# Revit family: RN 90077 Optifitt-Serra-Réduction
name_source: partatom
category: Rohrformteile
units: mm (PartAtom-declared; Revit-internal decimal feet)

## family parameters
Arbeitsebenenbasiert = Nein
Beim Laden mit Abzugskörper schneiden = Nein
Bemaßung runder Anschluss = Durchmesser verwenden
Gemeinsam genutzt = Nein
Immer vertikal = Ja
Teiletyp = Übergang

## types (12) — shared parameters
1.010.00.2 Blattnummer der Richtlinie = 29
1.010.00.3 Ausgabedatum (Monat) der Richtlinie = 201308
1.010.00.4 Herstellername = R. Nussbaum AG
1.010.00.5 Revisionsdatum der Datei = 20190521
1.010.00.6 Webadresse des Herstellers = http://www.nussbaum.ch
1.100.00.4 Produktbezeichnung = Versorgung
1.110.00.2 Index = 3
1.110.00.4 Produktbezeichnung = Optifitt-Serra
1.960/3L.00.8 Link (URL) = https://www.nussbaum.ch
29.700.00.4 Produktname = Optifitt-Serra-Reduktion
29.700.00.5 Produktkennung = 2
29.700.00.6 Querschnittsform = 1
29.700.00.7 Nennweitensystem = DN
29.700.00.8 Nenndrucksystem = PN
29.710.02.4 Nenndruck = 16
29.710.02.5 max. zul. Überdruck [hPa] = 1600
29.710.02.7 max. zul. Dauer-Betriebsdruck [hPa] = 1600
29.710.02.9 max. zul. Dauer-Betriebstemperatur [°C] = 90
Connector Visibility = Nein
EnclosingSpace Visibility = Nein

## per-type parameters (varying)
- DN=50x32: 1.800.00.3 TGA-Nummer=01900300000000000000000000000000000000000000000014000000000000000046; 1.800.00.4 Kommentarfeld=90077.40, Optifitt-Serra-Reduktion, DN=50x32, L=36, R=2, Rp=1¼; 1.810.00.3 Hersteller-Bestellnummer=90077.4; 1.810.00.4 DATANORM-Nummer=90077.4; 1.810.00.5 StLB-Nummer=214.537; 1.810.00.6 GTIN-Nummer=7612945680211; 29.710.02.10 Formstück-Gewicht [kg]=0.349; 29.710.02.3 Benennung=Optifitt-Serra-Reduktion, DN=50x32, L=36, R=2, Rp=1¼; CONNECTOR0_DIAMETER_dX_0r=32 mm; CONNECTOR0_dX_01=19 mm; CONNECTOR0_ref_dX=19 mm; CONNECTOR1_DIAMETER_dX_0r=50 mm; CONNECTOR1_dX_00=12 mm  [stored 0.0393701 ft]; CONNECTOR1_dX_01=36 mm; CONNECTOR1_ref_dX=36 mm; Hersteller=R. Nussbaum AG; Modell=90077.4; R. Nussbaum AG 90077.23 de Visibility=Nein; R. Nussbaum AG 90077.26 de Visibility=Nein; R. Nussbaum AG 90077.28 de Visibility=Nein; R. Nussbaum AG 90077.29 de Visibility=Nein; R. Nussbaum AG 90077.31 de Visibility=Nein; R. Nussbaum AG 90077.32 de Visibility=Nein; R. Nussbaum AG 90077.35 de Visibility=Nein; R. Nussbaum AG 90077.36 de Visibility=Nein; R. Nussbaum AG 90077.40 de Visibility=Ja; R. Nussbaum AG 90077.41 de Visibility=Nein; R. Nussbaum AG 90077.43 de Visibility=Nein; R. Nussbaum AG 90077.44 de Visibility=Nein; Typenkommentare=Optifitt-Serra-Réduction  DN=50x32; URL=https://www.nussbaum.ch
- DN=80x65: 1.800.00.3 TGA-Nummer=01900300000000000000000000000000000000000000000014000000000000000035; 1.800.00.4 Kommentarfeld=90077.44, Optifitt-Serra-Reduktion, DN=80x65, L=47, R=3, Rp=2½; 1.810.00.3 Hersteller-Bestellnummer=90077.44; 1.810.00.4 DATANORM-Nummer=90077.44; 1.810.00.6 GTIN-Nummer=7612945680242; 29.710.02.10 Formstück-Gewicht [kg]=0.757; 29.710.02.3 Benennung=Optifitt-Serra-Reduktion, DN=80x65, L=47, R=3, Rp=2½; CONNECTOR0_DIAMETER_dX_0r=65 mm; CONNECTOR0_dX_01=27 mm; CONNECTOR0_ref_dX=27 mm; CONNECTOR1_DIAMETER_dX_0r=80 mm; CONNECTOR1_dX_00=17 mm; CONNECTOR1_dX_01=47 mm; CONNECTOR1_ref_dX=47 mm; Hersteller=R. Nussbaum AG; Modell=90077.44; R. Nussbaum AG 90077.23 de Visibility=Nein; R. Nussbaum AG 90077.26 de Visibility=Nein; R. Nussbaum AG 90077.28 de Visibility=Nein; R. Nussbaum AG 90077.29 de Visibility=Nein; R. Nussbaum AG 90077.31 de Visibility=Nein; R. Nussbaum AG 90077.32 de Visibility=Nein; R. Nussbaum AG 90077.35 de Visibility=Nein; R. Nussbaum AG 90077.36 de Visibility=Nein; R. Nussbaum AG 90077.40 de Visibility=Nein; R. Nussbaum AG 90077.41 de Visibility=Nein; R. Nussbaum AG 90077.43 de Visibility=Nein; R. Nussbaum AG 90077.44 de Visibility=Ja; Typenkommentare=Optifitt-Serra-Réduction  DN=80x65; URL=https://www.nussbaum.ch
- DN=65x50: 1.800.00.3 TGA-Nummer=01900300000000000000000000000000000000000000000014000000000000000034; 1.800.00.4 Kommentarfeld=90077.43, Optifitt-Serra-Reduktion, DN=65x50, L=45, R=2½, Rp=2; 1.810.00.3 Hersteller-Bestellnummer=90077.43; 1.810.00.4 DATANORM-Nummer=90077.43; 1.810.00.5 StLB-Nummer=214.538; 1.810.00.6 GTIN-Nummer=7612945680235; 29.710.02.10 Formstück-Gewicht [kg]=0.629; 29.710.02.3 Benennung=Optifitt-Serra-Reduktion, DN=65x50, L=45, R=2½, Rp=2; CONNECTOR0_DIAMETER_dX_0r=50 mm; CONNECTOR0_dX_01=24 mm; CONNECTOR0_ref_dX=24 mm; CONNECTOR1_DIAMETER_dX_0r=65 mm; CONNECTOR1_dX_00=18 mm; CONNECTOR1_dX_01=45 mm  [stored 0.147638 ft]; CONNECTOR1_ref_dX=45 mm  [stored 0.147638 ft]; Hersteller=R. Nussbaum AG; Modell=90077.43; R. Nussbaum AG 90077.23 de Visibility=Nein; R. Nussbaum AG 90077.26 de Visibility=Nein; R. Nussbaum AG 90077.28 de Visibility=Nein; R. Nussbaum AG 90077.29 de Visibility=Nein; R. Nussbaum AG 90077.31 de Visibility=Nein; R. Nussbaum AG 90077.32 de Visibility=Nein; R. Nussbaum AG 90077.35 de Visibility=Nein; R. Nussbaum AG 90077.36 de Visibility=Nein; R. Nussbaum AG 90077.40 de Visibility=Nein; R. Nussbaum AG 90077.41 de Visibility=Nein; R. Nussbaum AG 90077.43 de Visibility=Ja; R. Nussbaum AG 90077.44 de Visibility=Nein; Typenkommentare=Optifitt-Serra-Réduction  DN=65x50; URL=https://www.nussbaum.ch
- DN=50x40: 1.800.00.3 TGA-Nummer=01900300000000000000000000000000000000000000000014000000000000000033; 1.800.00.4 Kommentarfeld=90077.41, Optifitt-Serra-Reduktion, DN=50x40, L=36, R=2, Rp=1½; 1.810.00.3 Hersteller-Bestellnummer=90077.41; 1.810.00.4 DATANORM-Nummer=90077.41; 1.810.00.5 StLB-Nummer=214.537; 1.810.00.6 GTIN-Nummer=7612945680228; 29.710.02.10 Formstück-Gewicht [kg]=0.295; 29.710.02.3 Benennung=Optifitt-Serra-Reduktion, DN=50x40, L=36, R=2, Rp=1½; CONNECTOR0_DIAMETER_dX_0r=40 mm; CONNECTOR0_dX_01=19 mm; CONNECTOR0_ref_dX=19 mm; CONNECTOR1_DIAMETER_dX_0r=50 mm; CONNECTOR1_dX_00=12 mm  [stored 0.0393701 ft]; CONNECTOR1_dX_01=36 mm; CONNECTOR1_ref_dX=36 mm; Hersteller=R. Nussbaum AG; Modell=90077.41; R. Nussbaum AG 90077.23 de Visibility=Nein; R. Nussbaum AG 90077.26 de Visibility=Nein; R. Nussbaum AG 90077.28 de Visibility=Nein; R. Nussbaum AG 90077.29 de Visibility=Nein; R. Nussbaum AG 90077.31 de Visibility=Nein; R. Nussbaum AG 90077.32 de Visibility=Nein; R. Nussbaum AG 90077.35 de Visibility=Nein; R. Nussbaum AG 90077.36 de Visibility=Nein; R. Nussbaum AG 90077.40 de Visibility=Nein; R. Nussbaum AG 90077.41 de Visibility=Ja; R. Nussbaum AG 90077.43 de Visibility=Nein; R. Nussbaum AG 90077.44 de Visibility=Nein; Typenkommentare=Optifitt-Serra-Réduction  DN=50x40; URL=https://www.nussbaum.ch
- DN=40x32: 1.800.00.3 TGA-Nummer=01900300000000000000000000000000000000000000000014000000000000000032; 1.800.00.4 Kommentarfeld=90077.36, Optifitt-Serra-Reduktion, DN=40x32, L=36, R=1½, Rp=1¼; 1.810.00.3 Hersteller-Bestellnummer=90077.36; 1.810.00.4 DATANORM-Nummer=90077.36; 1.810.00.5 StLB-Nummer=214.536; 1.810.00.6 GTIN-Nummer=7612945680204; 29.710.02.10 Formstück-Gewicht [kg]=0.2; 29.710.02.3 Benennung=Optifitt-Serra-Reduktion, DN=40x32, L=36, R=1½, Rp=1¼; CONNECTOR0_DIAMETER_dX_0r=32 mm; CONNECTOR0_dX_01=19 mm; CONNECTOR0_ref_dX=19 mm; CONNECTOR1_DIAMETER_dX_0r=40 mm; CONNECTOR1_dX_00=17 mm; CONNECTOR1_dX_01=36 mm; CONNECTOR1_ref_dX=36 mm; Hersteller=R. Nussbaum AG; Modell=90077.36; R. Nussbaum AG 90077.23 de Visibility=Nein; R. Nussbaum AG 90077.26 de Visibility=Nein; R. Nussbaum AG 90077.28 de Visibility=Nein; R. Nussbaum AG 90077.29 de Visibility=Nein; R. Nussbaum AG 90077.31 de Visibility=Nein; R. Nussbaum AG 90077.32 de Visibility=Nein; R. Nussbaum AG 90077.35 de Visibility=Nein; R. Nussbaum AG 90077.36 de Visibility=Ja; R. Nussbaum AG 90077.40 de Visibility=Nein; R. Nussbaum AG 90077.41 de Visibility=Nein; R. Nussbaum AG 90077.43 de Visibility=Nein; R. Nussbaum AG 90077.44 de Visibility=Nein; Typenkommentare=Optifitt-Serra-Réduction  DN=40x32; URL=https://www.nussbaum.ch
- DN=40x25: 1.800.00.3 TGA-Nummer=01900300000000000000000000000000000000000000000014000000000000000031; 1.800.00.4 Kommentarfeld=90077.35, Optifitt-Serra-Reduktion, DN=40x25, L=36, R=1½, Rp=1; 1.810.00.3 Hersteller-Bestellnummer=90077.35; 1.810.00.4 DATANORM-Nummer=90077.35; 1.810.00.5 StLB-Nummer=214.535; 1.810.00.6 GTIN-Nummer=7612945680198; 29.710.02.10 Formstück-Gewicht [kg]=0.001; 29.710.02.3 Benennung=Optifitt-Serra-Reduktion, DN=40x25, L=36, R=1½, Rp=1; CONNECTOR0_DIAMETER_dX_0r=25 mm  [stored 0.082021 ft]; CONNECTOR0_dX_01=17 mm; CONNECTOR0_ref_dX=17 mm; CONNECTOR1_DIAMETER_dX_0r=40 mm; CONNECTOR1_dX_00=17 mm; CONNECTOR1_dX_01=36 mm; CONNECTOR1_ref_dX=36 mm; Hersteller=R. Nussbaum AG; Modell=90077.35; R. Nussbaum AG 90077.23 de Visibility=Nein; R. Nussbaum AG 90077.26 de Visibility=Nein; R. Nussbaum AG 90077.28 de Visibility=Nein; R. Nussbaum AG 90077.29 de Visibility=Nein; R. Nussbaum AG 90077.31 de Visibility=Nein; R. Nussbaum AG 90077.32 de Visibility=Nein; R. Nussbaum AG 90077.35 de Visibility=Ja; R. Nussbaum AG 90077.36 de Visibility=Nein; R. Nussbaum AG 90077.40 de Visibility=Nein; R. Nussbaum AG 90077.41 de Visibility=Nein; R. Nussbaum AG 90077.43 de Visibility=Nein; R. Nussbaum AG 90077.44 de Visibility=Nein; Typenkommentare=Optifitt-Serra-Réduction  DN=40x25; URL=https://www.nussbaum.ch
- DN=32x25: 1.800.00.3 TGA-Nummer=01900300000000000000000000000000000000000000000014000000000000000030; 1.800.00.4 Kommentarfeld=90077.32, Optifitt-Serra-Reduktion, DN=32x25, L=30, R=1¼, Rp=1; 1.810.00.3 Hersteller-Bestellnummer=90077.32; 1.810.00.4 DATANORM-Nummer=90077.32; 1.810.00.5 StLB-Nummer=214.535; 1.810.00.6 GTIN-Nummer=7612945680259; 29.710.02.10 Formstück-Gewicht [kg]=0.139; 29.710.02.3 Benennung=Optifitt-Serra-Reduktion, DN=32x25, L=30, R=1¼, Rp=1; CONNECTOR0_DIAMETER_dX_0r=25 mm  [stored 0.082021 ft]; CONNECTOR0_dX_01=17 mm; CONNECTOR0_ref_dX=17 mm; CONNECTOR1_DIAMETER_dX_0r=32 mm; CONNECTOR1_dX_00=11 mm; CONNECTOR1_dX_01=30 mm; CONNECTOR1_ref_dX=30 mm; Hersteller=R. Nussbaum AG; Modell=90077.32; R. Nussbaum AG 90077.23 de Visibility=Nein; R. Nussbaum AG 90077.26 de Visibility=Nein; R. Nussbaum AG 90077.28 de Visibility=Nein; R. Nussbaum AG 90077.29 de Visibility=Nein; R. Nussbaum AG 90077.31 de Visibility=Nein; R. Nussbaum AG 90077.32 de Visibility=Ja; R. Nussbaum AG 90077.35 de Visibility=Nein; R. Nussbaum AG 90077.36 de Visibility=Nein; R. Nussbaum AG 90077.40 de Visibility=Nein; R. Nussbaum AG 90077.41 de Visibility=Nein; R. Nussbaum AG 90077.43 de Visibility=Nein; R. Nussbaum AG 90077.44 de Visibility=Nein; Typenkommentare=Optifitt-Serra-Réduction  DN=32x25; URL=https://www.nussbaum.ch
- DN=32x20: 1.800.00.3 TGA-Nummer=01900300000000000000000000000000000000000000000014000000000000000029; 1.800.00.4 Kommentarfeld=90077.31, Optifitt-Serra-Reduktion, DN=32x20, L=30, R=1¼, Rp=¾; 1.810.00.3 Hersteller-Bestellnummer=90077.31; 1.810.00.4 DATANORM-Nummer=90077.31; 1.810.00.5 StLB-Nummer=214.535; 1.810.00.6 GTIN-Nummer=7612945680181; 29.710.02.10 Formstück-Gewicht [kg]=0.175; 29.710.02.3 Benennung=Optifitt-Serra-Reduktion, DN=32x20, L=30, R=1¼, Rp=¾; CONNECTOR0_DIAMETER_dX_0r=20 mm; CONNECTOR0_dX_01=15 mm  [stored 0.0492126 ft]; CONNECTOR0_ref_dX=15 mm  [stored 0.0492126 ft]; CONNECTOR1_DIAMETER_dX_0r=32 mm; CONNECTOR1_dX_00=11 mm; CONNECTOR1_dX_01=30 mm; CONNECTOR1_ref_dX=30 mm; Hersteller=R. Nussbaum AG; Modell=90077.31; R. Nussbaum AG 90077.23 de Visibility=Nein; R. Nussbaum AG 90077.26 de Visibility=Nein; R. Nussbaum AG 90077.28 de Visibility=Nein; R. Nussbaum AG 90077.29 de Visibility=Nein; R. Nussbaum AG 90077.31 de Visibility=Ja; R. Nussbaum AG 90077.32 de Visibility=Nein; R. Nussbaum AG 90077.35 de Visibility=Nein; R. Nussbaum AG 90077.36 de Visibility=Nein; R. Nussbaum AG 90077.40 de Visibility=Nein; R. Nussbaum AG 90077.41 de Visibility=Nein; R. Nussbaum AG 90077.43 de Visibility=Nein; R. Nussbaum AG 90077.44 de Visibility=Nein; Typenkommentare=Optifitt-Serra-Réduction  DN=32x20; URL=https://www.nussbaum.ch
- DN=25x20: 1.800.00.3 TGA-Nummer=01900300000000000000000000000000000000000000000014000000000000000028; 1.800.00.4 Kommentarfeld=90077.29, Optifitt-Serra-Reduktion, DN=25x20, L=27, R=1, Rp=¾; 1.810.00.3 Hersteller-Bestellnummer=90077.29; 1.810.00.4 DATANORM-Nummer=90077.29; 1.810.00.5 StLB-Nummer=214.534; 1.810.00.6 GTIN-Nummer=7612945680174; 29.710.02.10 Formstück-Gewicht [kg]=0.074; 29.710.02.3 Benennung=Optifitt-Serra-Reduktion, DN=25x20, L=27, R=1, Rp=¾; CONNECTOR0_DIAMETER_dX_0r=20 mm; CONNECTOR0_dX_01=15 mm  [stored 0.0492126 ft]; CONNECTOR0_ref_dX=15 mm  [stored 0.0492126 ft]; CONNECTOR1_DIAMETER_dX_0r=25 mm  [stored 0.082021 ft]; CONNECTOR1_dX_00=10 mm  [stored 0.0328084 ft]; CONNECTOR1_dX_01=27 mm; CONNECTOR1_ref_dX=27 mm; Hersteller=R. Nussbaum AG; Modell=90077.29; R. Nussbaum AG 90077.23 de Visibility=Nein; R. Nussbaum AG 90077.26 de Visibility=Nein; R. Nussbaum AG 90077.28 de Visibility=Nein; R. Nussbaum AG 90077.29 de Visibility=Ja; R. Nussbaum AG 90077.31 de Visibility=Nein; R. Nussbaum AG 90077.32 de Visibility=Nein; R. Nussbaum AG 90077.35 de Visibility=Nein; R. Nussbaum AG 90077.36 de Visibility=Nein; R. Nussbaum AG 90077.40 de Visibility=Nein; R. Nussbaum AG 90077.41 de Visibility=Nein; R. Nussbaum AG 90077.43 de Visibility=Nein; R. Nussbaum AG 90077.44 de Visibility=Nein; Typenkommentare=Optifitt-Serra-Réduction  DN=25x20; URL=https://www.nussbaum.ch
- DN=25x15: 1.800.00.3 TGA-Nummer=01900300000000000000000000000000000000000000000014000000000000000027; 1.800.00.4 Kommentarfeld=90077.28, Optifitt-Serra-Reduktion, DN=25x15, L=27, R=1, Rp=½; 1.810.00.3 Hersteller-Bestellnummer=90077.28; 1.810.00.4 DATANORM-Nummer=90077.28; 1.810.00.5 StLB-Nummer=214.534; 1.810.00.6 GTIN-Nummer=7612945680167; 29.710.02.10 Formstück-Gewicht [kg]=0.089; 29.710.02.3 Benennung=Optifitt-Serra-Reduktion, DN=25x15, L=27, R=1, Rp=½; CONNECTOR0_DIAMETER_dX_0r=15 mm  [stored 0.0492126 ft]; CONNECTOR0_dX_01=13 mm; CONNECTOR0_ref_dX=13 mm; CONNECTOR1_DIAMETER_dX_0r=25 mm  [stored 0.082021 ft]; CONNECTOR1_dX_00=10 mm  [stored 0.0328084 ft]; CONNECTOR1_dX_01=27 mm; CONNECTOR1_ref_dX=27 mm; Hersteller=R. Nussbaum AG; Modell=90077.28; R. Nussbaum AG 90077.23 de Visibility=Nein; R. Nussbaum AG 90077.26 de Visibility=Nein; R. Nussbaum AG 90077.28 de Visibility=Ja; R. Nussbaum AG 90077.29 de Visibility=Nein; R. Nussbaum AG 90077.31 de Visibility=Nein; R. Nussbaum AG 90077.32 de Visibility=Nein; R. Nussbaum AG 90077.35 de Visibility=Nein; R. Nussbaum AG 90077.36 de Visibility=Nein; R. Nussbaum AG 90077.40 de Visibility=Nein; R. Nussbaum AG 90077.41 de Visibility=Nein; R. Nussbaum AG 90077.43 de Visibility=Nein; R. Nussbaum AG 90077.44 de Visibility=Nein; Typenkommentare=Optifitt-Serra-Réduction  DN=25x15; URL=https://www.nussbaum.ch
- DN=20x15: 1.800.00.3 TGA-Nummer=01900300000000000000000000000000000000000000000014000000000000000026; 1.800.00.4 Kommentarfeld=90077.26, Optifitt-Serra-Reduktion, DN=20x15, L=24, R=¾, Rp=½; 1.810.00.3 Hersteller-Bestellnummer=90077.26; 1.810.00.4 DATANORM-Nummer=90077.26; 1.810.00.5 StLB-Nummer=214.533; 1.810.00.6 GTIN-Nummer=7612945680150; 29.710.02.10 Formstück-Gewicht [kg]=0.055; 29.710.02.3 Benennung=Optifitt-Serra-Reduktion, DN=20x15, L=24, R=¾, Rp=½; CONNECTOR0_DIAMETER_dX_0r=15 mm  [stored 0.0492126 ft]; CONNECTOR0_dX_01=13 mm; CONNECTOR0_ref_dX=13 mm; CONNECTOR1_DIAMETER_dX_0r=20 mm; CONNECTOR1_dX_00=9 mm  [stored 0.0295276 ft]; CONNECTOR1_dX_01=24 mm; CONNECTOR1_ref_dX=24 mm; R. Nussbaum AG 90077.23 de Visibility=Nein; R. Nussbaum AG 90077.26 de Visibility=Ja; R. Nussbaum AG 90077.28 de Visibility=Nein; R. Nussbaum AG 90077.29 de Visibility=Nein; R. Nussbaum AG 90077.31 de Visibility=Nein; R. Nussbaum AG 90077.32 de Visibility=Nein; R. Nussbaum AG 90077.35 de Visibility=Nein; R. Nussbaum AG 90077.36 de Visibility=Nein; R. Nussbaum AG 90077.40 de Visibility=Nein; R. Nussbaum AG 90077.41 de Visibility=Nein; R. Nussbaum AG 90077.43 de Visibility=Nein; R. Nussbaum AG 90077.44 de Visibility=Nein
- DN=15x12: 1.800.00.3 TGA-Nummer=01900300000000000000000000000000000000000000000014000000000000000025; 1.800.00.4 Kommentarfeld=90077.23, Optifitt-Serra-Reduktion, DN=15x12, L=21, R=½, Rp=3/8; 1.810.00.3 Hersteller-Bestellnummer=90077.23; 1.810.00.4 DATANORM-Nummer=90077.23; 1.810.00.5 StLB-Nummer=214.532; 1.810.00.6 GTIN-Nummer=7612945680143; 29.710.02.10 Formstück-Gewicht [kg]=0.032; 29.710.02.3 Benennung=Optifitt-Serra-Reduktion, DN=15x12, L=21, R=½, Rp=3/8; CONNECTOR0_DIAMETER_dX_0r=12 mm  [stored 0.0393701 ft]; CONNECTOR0_dX_01=10 mm  [stored 0.0328084 ft]; CONNECTOR0_ref_dX=10 mm  [stored 0.0328084 ft]; CONNECTOR1_DIAMETER_dX_0r=15 mm  [stored 0.0492126 ft]; CONNECTOR1_dX_00=8 mm  [stored 0.0262467 ft]; CONNECTOR1_dX_01=21 mm; CONNECTOR1_ref_dX=21 mm; Hersteller=R. Nussbaum AG; Modell=90077.23; R. Nussbaum AG 90077.23 de Visibility=Ja; R. Nussbaum AG 90077.26 de Visibility=Nein; R. Nussbaum AG 90077.28 de Visibility=Nein; R. Nussbaum AG 90077.29 de Visibility=Nein; R. Nussbaum AG 90077.31 de Visibility=Nein; R. Nussbaum AG 90077.32 de Visibility=Nein; R. Nussbaum AG 90077.35 de Visibility=Nein; R. Nussbaum AG 90077.36 de Visibility=Nein; R. Nussbaum AG 90077.40 de Visibility=Nein; R. Nussbaum AG 90077.41 de Visibility=Nein; R. Nussbaum AG 90077.43 de Visibility=Nein; R. Nussbaum AG 90077.44 de Visibility=Nein; Typenkommentare=Optifitt-Serra-Réduction  DN=15x12; URL=https://www.nussbaum.ch

note: [stored X ft] marks values corroborated as IEEE doubles in the binary element streams (Revit-internal decimal feet)

## geometry (parser evidence)
native form markers: Sweep x1
no freeform markers — native parametric forms only
